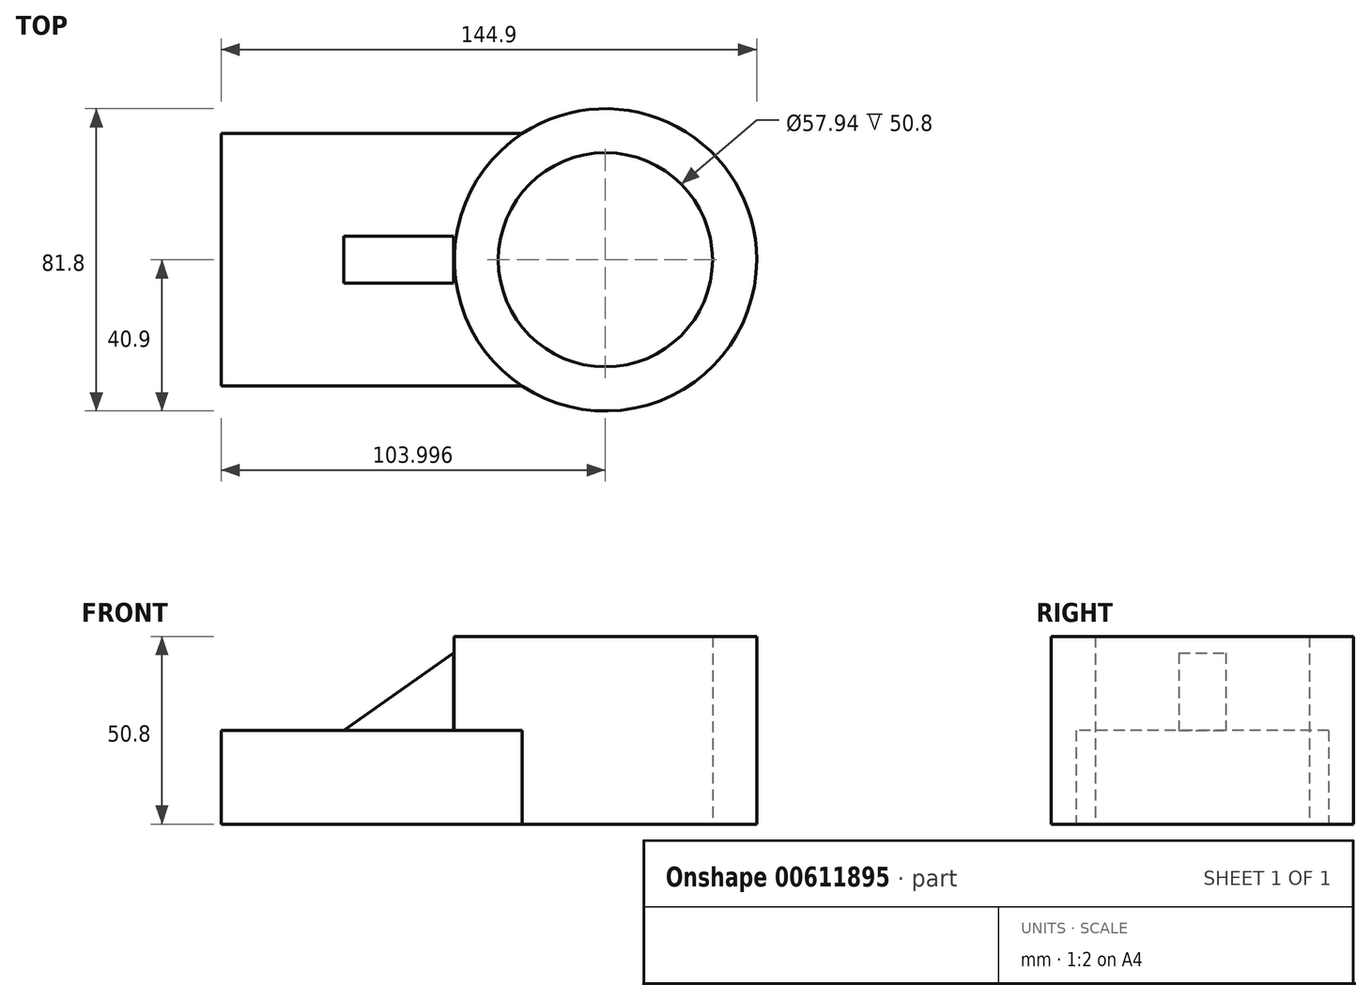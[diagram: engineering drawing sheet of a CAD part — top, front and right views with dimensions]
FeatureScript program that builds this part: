
annotation { "Feature Type Name" : "Feature", "Feature Type Description" : "" }
export const myFeature = defineFeature(function(context is Context, id is Id, definition is map)
    precondition{}
    {
        {
            var Q0;
            Q0=qCreatedBy(makeId("Top.planeOp"),FACE);
            var sketch = newSketch(context, id + "F0", { "sketchPlane" : qUnion([Q0])});
            skLineSegment(sketch, "E0.bottom", {"start": v(29.49, 34.15) * mm, "end": v(-52, 34.15) * mm});
            skLineSegment(sketch, "E0.top", {"start": v(29.49, -34.15) * mm, "end": v(-52, -34.15) * mm});
            skLineSegment(sketch, "E0.right", {"start": v(-52, 34.15) * mm, "end": v(-52, -34.15) * mm});
            skPoint(sketch, "E0.middle", {"position": v(0, 0) * mm});
            skCircle(sketch, "E1", {"center": v(52, 0) * mm, "radius": 40.9 * mm});
            skCircle(sketch, "E2", {"center": v(52, 0) * mm, "radius": 28.97 * mm});
            skPoint(sketch, "E3.orphan", {"position": v(52, -34.15) * mm});
            skPoint(sketch, "E4.orphan", {"position": v(52, 34.15) * mm});
            skSolve(sketch);
        }
        {
            var Q0;
            Q0=makeQuery(id+"F0.imprint","IMPRINT",FACE,{"disambiguationData":[TD([[makeQuery(id+"F0.imprint","IMPRINT",EDGE,{"derivedFrom":sQuery(id+"F0.wireOp",EDGE,"E2")}),-1.0]])]});
            extrude(context, id + "F1", {"entities" : qUnion([Q0]), "depth" : 50.8 * mm, "offsetDistance" : 25.4 * mm});
        }
        {
            var Q0;
            Q0 = qSketchRegion(id + "F0", true);
            extrude(context, id + "F2", {"entities" : qUnion([Q0]), "operationType" : NewBodyOperationType.ADD, "depth" : 25.4 * mm, "offsetDistance" : 25.4 * mm});
        }
        {
            var Q0;
            Q0=qCreatedBy(makeId("Front.planeOp"),FACE);
            var sketch = newSketch(context, id + "F3", { "sketchPlane" : qUnion([Q0])});
            skLineSegment(sketch, "E5.top", {"start": v(10.9, 20.82) * mm, "end": v(-25.34, 20.82) * mm});
            skLineSegment(sketch, "E5.left", {"start": v(10.9, 46.38) * mm, "end": v(10.9, 20.82) * mm});
            skLineSegment(sketch, "E6", {"start": v(10.9, 46.38) * mm, "end": v(-25.34, 20.82) * mm});
            skSolve(sketch);
        }
        {
            var Q0;
            Q0 = qSketchRegion(id + "F3", true);
            extrude(context, id + "F4", {"entities" : qUnion([Q0]), "operationType" : NewBodyOperationType.ADD, "endBound" : BoundingType.SYMMETRIC, "depth" : 12.7 * mm, "offsetDistance" : 25.4 * mm});
        }
    });
